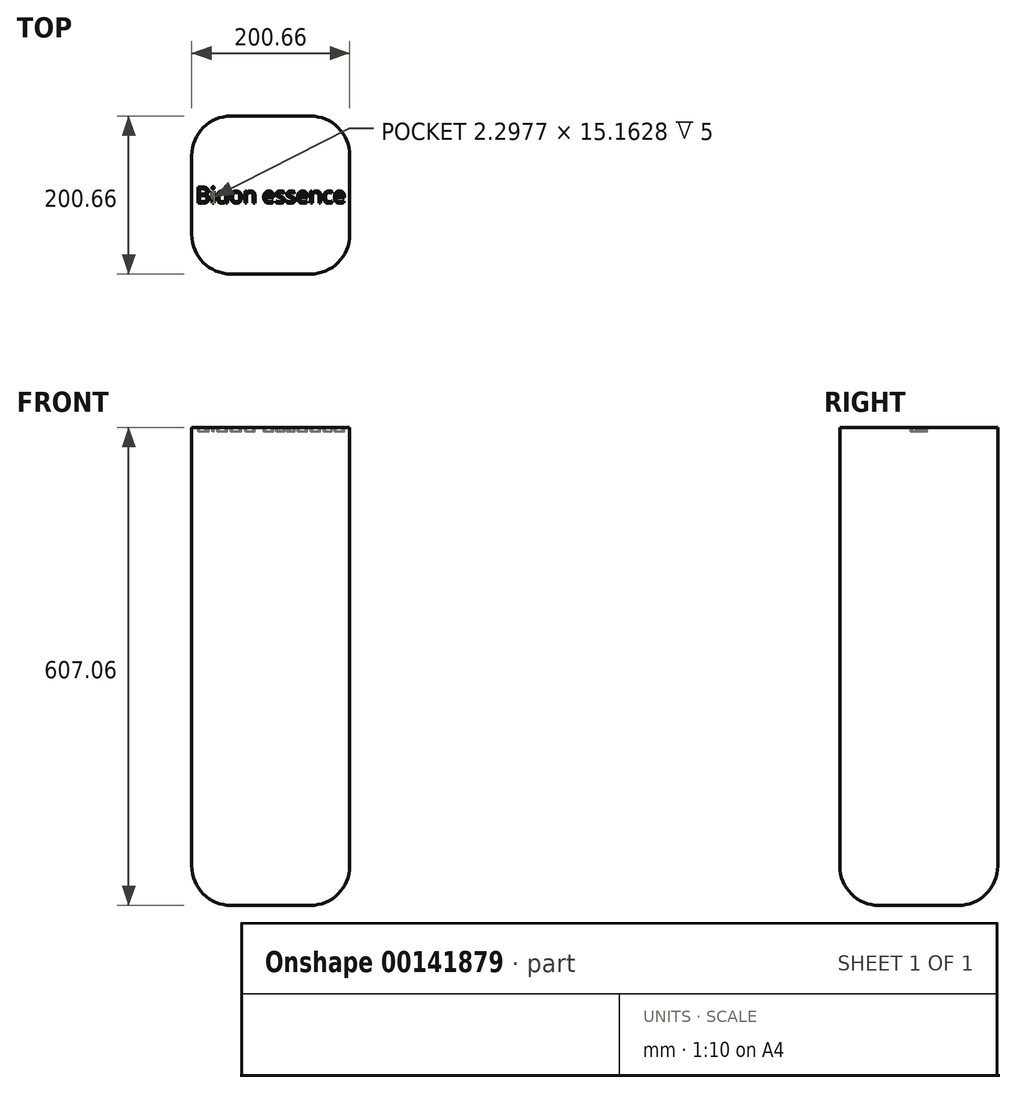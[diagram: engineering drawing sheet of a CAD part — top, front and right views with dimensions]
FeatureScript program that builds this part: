
annotation { "Feature Type Name" : "Feature", "Feature Type Description" : "" }
export const myFeature = defineFeature(function(context is Context, id is Id, definition is map)
    precondition{}
    {
        {
            var Q0;
            Q0=qCreatedBy(makeId("Top.planeOp"),FACE);
            var sketch = newSketch(context, id + "F0", { "sketchPlane" : qUnion([Q0])});
            skLineSegment(sketch, "E0.bottom", {"start": v(100.33, -100.33) * mm, "end": v(-100.33, -100.33) * mm});
            skLineSegment(sketch, "E0.top", {"start": v(100.33, 100.33) * mm, "end": v(-100.33, 100.33) * mm});
            skLineSegment(sketch, "E0.left", {"start": v(100.33, -100.33) * mm, "end": v(100.33, 100.33) * mm});
            skLineSegment(sketch, "E0.right", {"start": v(-100.33, -100.33) * mm, "end": v(-100.33, 100.33) * mm});
            skPoint(sketch, "E0.middle", {"position": v(0, 0) * mm});
            skSolve(sketch);
        }
        {
            var Q0;
            Q0=makeQuery(id+"F0.imprint","IMPRINT",FACE,{"disambiguationData":[TD([[makeQuery(id+"F0.imprint","IMPRINT",EDGE,{"derivedFrom":sQuery(id+"F0.wireOp",EDGE,"E0.bottom")}),-1.0]])]});
            extrude(context, id + "F1", {"entities" : qUnion([Q0]), "depth" : 607.06 * mm});
        }
        {
            var Q0;
            Q0=makeQuery(id+"F1.opExtrude","CAP_FACE",FACE,{"disambiguationData":[OSD([sQuery(id+"F0.wireOp",EDGE,"E0.bottom"),sQuery(id+"F0.wireOp",EDGE,"E0.top"),sQuery(id+"F0.wireOp",EDGE,"E0.left"),sQuery(id+"F0.wireOp",EDGE,"E0.right")])],"isStart":false});
            var sketch = newSketch(context, id + "F2", { "sketchPlane" : qUnion([Q0])});
            skText(sketch, "E1", { "text": "Bidon essence", "fontName": "OpenSans-Regular.ttf"});
            skPoint(sketch, "E2", {"position": v(0, 0) * mm});
            const initialGuessF2  = {"E1": [-0.09533, -0.0102, 1, 0, 0.0204]};
            skSetInitialGuess(sketch, initialGuessF2);
            skSolve(sketch);
        }
        {
            var Q0;
            Q0 = qSketchRegion(id + "F2", true);
            extrude(context, id + "F3", {"entities" : qUnion([Q0]), "operationType" : NewBodyOperationType.REMOVE, "oppositeDirection" : true, "depth" : 5 * mm});
        }
        {
            var Q0;
            Q0=makeQuery(id+"F1.opExtrude","SWEPT_EDGE",EDGE,{"disambiguationData":[OSD([sQuery(id+"F0.wireOp",EDGE,"E0.bottom"),sQuery(id+"F0.wireOp",EDGE,"E0.left")])]});
            var Q1;
            Q1=makeQuery(id+"F1.opExtrude","SWEPT_EDGE",EDGE,{"disambiguationData":[OSD([sQuery(id+"F0.wireOp",EDGE,"E0.top"),sQuery(id+"F0.wireOp",EDGE,"E0.left")])]});
            var Q2;
            Q2=makeQuery(id+"F1.opExtrude","SWEPT_EDGE",EDGE,{"disambiguationData":[OSD([sQuery(id+"F0.wireOp",EDGE,"E0.bottom"),sQuery(id+"F0.wireOp",EDGE,"E0.right")])]});
            var Q3;
            Q3=makeQuery(id+"F1.opExtrude","SWEPT_EDGE",EDGE,{"disambiguationData":[OSD([sQuery(id+"F0.wireOp",EDGE,"E0.top"),sQuery(id+"F0.wireOp",EDGE,"E0.right")])]});
            var Q4;
            Q4=makeQuery(id+"F1.opExtrude","CAP_FACE",FACE,{"disambiguationData":[OSD([sQuery(id+"F0.wireOp",EDGE,"E0.bottom"),sQuery(id+"F0.wireOp",EDGE,"E0.top"),sQuery(id+"F0.wireOp",EDGE,"E0.left"),sQuery(id+"F0.wireOp",EDGE,"E0.right")])],"isStart":true});
            fillet(context, id + "F4", {"entities" : qUnion([Q0, Q1, Q2, Q3, Q4]), "radius" : 50 * mm, "tangentPropagation" : true, "allowEdgeOverflow" : false});
        }
    });
